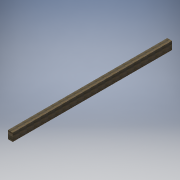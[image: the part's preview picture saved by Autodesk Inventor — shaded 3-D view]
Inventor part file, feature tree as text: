
AUTODESK INVENTOR PART (.ipt)
format: ipt  version: 2017 (Build 210142000, 142)  size: 98,816 bytes
history: native  units: mm
features: extrude x1, sketch x1
ambient origin geometry x8: Origin, YZ Plane, XZ Plane, XY Plane, X Axis, Y Axis, Z Axis, Center Point
bodies: Volumenkörper1 (feature_tree)
feature tree (2):
  extrude  "Extrusion1"  Depth=100.0mm
  sketch  "Skizze2"  dims[d2=60.0mm d3=100.0mm d4=2000.0mm d5=0.0mm]
